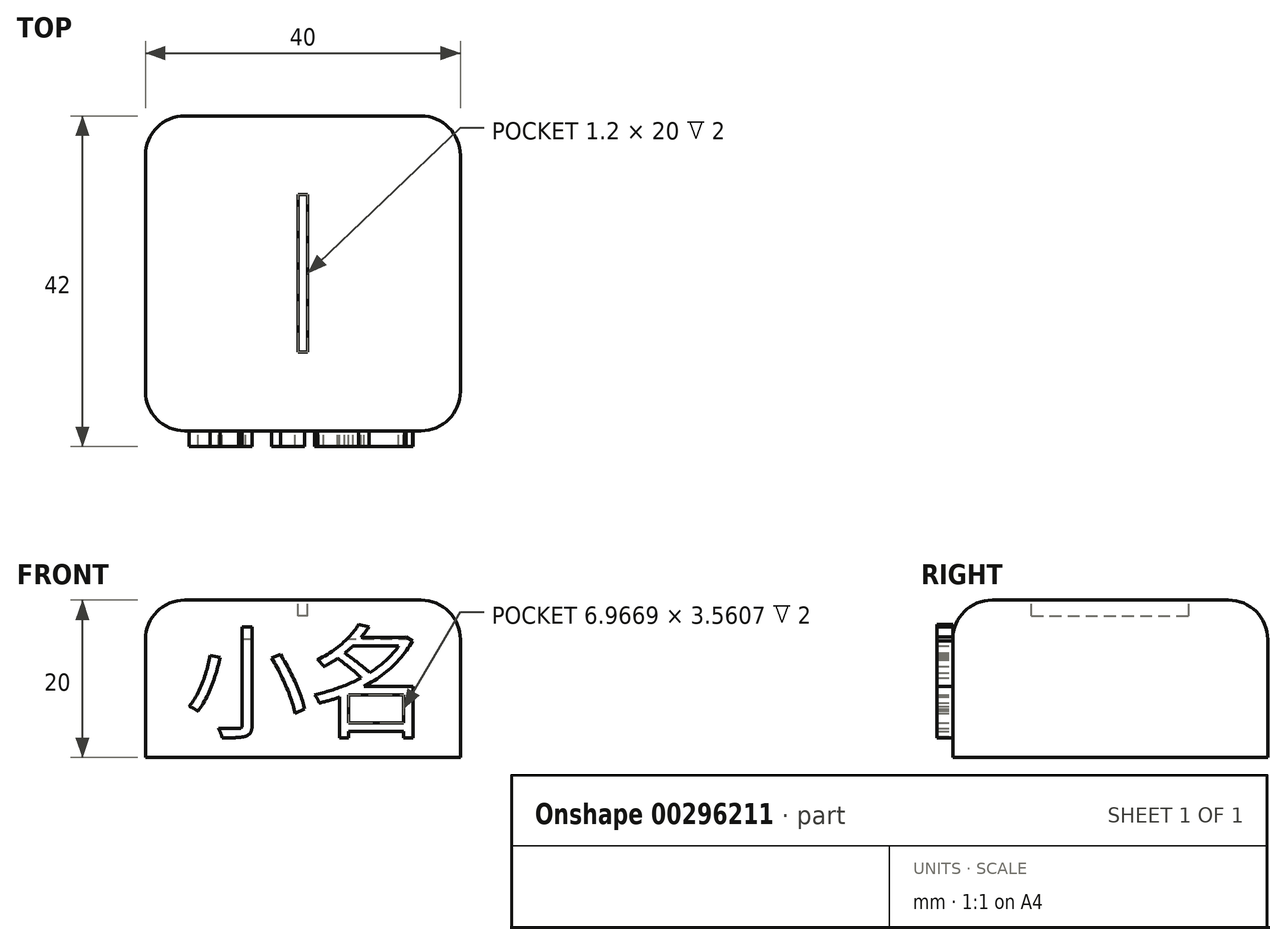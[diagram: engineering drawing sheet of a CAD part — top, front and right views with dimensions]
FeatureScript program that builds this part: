
annotation { "Feature Type Name" : "Feature", "Feature Type Description" : "" }
export const myFeature = defineFeature(function(context is Context, id is Id, definition is map)
    precondition{}
    {
        {
            var Q0;
            Q0=qCreatedBy(makeId("Top.planeOp"),FACE);
            var sketch = newSketch(context, id + "F0", { "sketchPlane" : qUnion([Q0])});
            skLineSegment(sketch, "E0.bottom", {"start": v(20, -20) * mm, "end": v(-20, -20) * mm});
            skLineSegment(sketch, "E0.top", {"start": v(20, 20) * mm, "end": v(-20, 20) * mm});
            skLineSegment(sketch, "E0.left", {"start": v(20, -20) * mm, "end": v(20, 20) * mm});
            skLineSegment(sketch, "E0.right", {"start": v(-20, -20) * mm, "end": v(-20, 20) * mm});
            skPoint(sketch, "E0.middle", {"position": v(0, 0) * mm});
            skLineSegment(sketch, "E1.bottom", {"start": v(0.6, -10) * mm, "end": v(-0.6, -10) * mm});
            skLineSegment(sketch, "E1.top", {"start": v(0.6, 10) * mm, "end": v(-0.6, 10) * mm});
            skLineSegment(sketch, "E1.left", {"start": v(0.6, -10) * mm, "end": v(0.6, 10) * mm});
            skLineSegment(sketch, "E1.right", {"start": v(-0.6, -10) * mm, "end": v(-0.6, 10) * mm});
            skSolve(sketch);
        }
        {
            var Q0;
            Q0=makeQuery(id+"F0.imprint","IMPRINT",FACE,{"disambiguationData":[TD([[makeQuery(id+"F0.imprint","IMPRINT",EDGE,{"derivedFrom":sQuery(id+"F0.wireOp",EDGE,"E0.bottom")}),-1.0]])]});
            var Q1;
            Q1=makeQuery(id+"F0.imprint","IMPRINT",FACE,{"disambiguationData":[TD([[makeQuery(id+"F0.imprint","IMPRINT",EDGE,{"derivedFrom":sQuery(id+"F0.wireOp",EDGE,"E1.bottom")}),-1.0]])]});
            extrude(context, id + "F1", {"entities" : qUnion([Q0, Q1]), "oppositeDirection" : true, "depth" : 20 * mm});
        }
        {
            var Q0;
            Q0=makeQuery(id+"F0.imprint","IMPRINT",FACE,{"disambiguationData":[TD([[makeQuery(id+"F0.imprint","IMPRINT",EDGE,{"derivedFrom":sQuery(id+"F0.wireOp",EDGE,"E1.bottom")}),-1.0]])]});
            extrude(context, id + "F2", {"entities" : qUnion([Q0]), "operationType" : NewBodyOperationType.REMOVE, "oppositeDirection" : true, "depth" : 2 * mm});
        }
        {
            var Q0;
            Q0=makeQuery(id+"F2.boolean.opBoolean","COPY",EDGE,{"derivedFrom":makeQuery(id+"F2.opExtrude","CAP_EDGE",EDGE,{"disambiguationData":[OSD([sQuery(id+"F0.wireOp",EDGE,"E1.left")])],"isStart":true})});
            var Q1;
            Q1=makeQuery(id+"F2.boolean.opBoolean","COPY",EDGE,{"derivedFrom":makeQuery(id+"F2.opExtrude","CAP_EDGE",EDGE,{"disambiguationData":[OSD([sQuery(id+"F0.wireOp",EDGE,"E1.right")])],"isStart":true})});
            var Q2;
            Q2=makeQuery(id+"F1.opExtrude","SWEPT_EDGE",EDGE,{"disambiguationData":[OSD([sQuery(id+"F0.wireOp",EDGE,"E0.bottom"),sQuery(id+"F0.wireOp",EDGE,"E0.left")])]});
            var Q3;
            Q3=makeQuery(id+"F1.opExtrude","SWEPT_EDGE",EDGE,{"disambiguationData":[OSD([sQuery(id+"F0.wireOp",EDGE,"E0.top"),sQuery(id+"F0.wireOp",EDGE,"E0.left")])]});
            var Q4;
            Q4=makeQuery(id+"F1.opExtrude","CAP_EDGE",EDGE,{"disambiguationData":[OSD([sQuery(id+"F0.wireOp",EDGE,"E0.left")])],"isStart":true});
            var Q5;
            Q5=makeQuery(id+"F1.opExtrude","SWEPT_EDGE",EDGE,{"disambiguationData":[OSD([sQuery(id+"F0.wireOp",EDGE,"E0.bottom"),sQuery(id+"F0.wireOp",EDGE,"E0.right")])]});
            var Q6;
            Q6=makeQuery(id+"F1.opExtrude","SWEPT_EDGE",EDGE,{"disambiguationData":[OSD([sQuery(id+"F0.wireOp",EDGE,"E0.top"),sQuery(id+"F0.wireOp",EDGE,"E0.right")])]});
            var Q7;
            Q7=makeQuery(id+"F1.opExtrude","CAP_EDGE",EDGE,{"disambiguationData":[OSD([sQuery(id+"F0.wireOp",EDGE,"E0.top")])],"isStart":true});
            var Q8;
            Q8=makeQuery(id+"F1.opExtrude","CAP_EDGE",EDGE,{"disambiguationData":[OSD([sQuery(id+"F0.wireOp",EDGE,"E0.right")])],"isStart":true});
            var Q9;
            Q9=makeQuery(id+"F1.opExtrude","CAP_EDGE",EDGE,{"disambiguationData":[OSD([sQuery(id+"F0.wireOp",EDGE,"E0.bottom")])],"isStart":true});
            fillet(context, id + "F3", {"entities" : qUnion([Q0, Q1, Q2, Q3, Q4, Q5, Q6, Q7, Q8, Q9]), "radius" : 5 * mm, "tangentPropagation" : true, "allowEdgeOverflow" : false});
        }
        {
            var Q0;
            Q0=makeQuery(id+"F1.opExtrude","SWEPT_FACE",FACE,{"disambiguationData":[OSD([sQuery(id+"F0.wireOp",EDGE,"E0.bottom")])]});
            var sketch = newSketch(context, id + "F4", { "sketchPlane" : qUnion([Q0])});
            skText(sketch, "E2", { "text": "小名", "fontName": "NotoSansCJKtc-Regular.otf"});
            const initialGuessF4  = {"E2": [-0.015, -0.0163, 1, 0, 0.0113]};
            skSetInitialGuess(sketch, initialGuessF4);
            skSolve(sketch);
        }
        {
            var Q0;
            {var subQ0=sQuery(id+"F4.wireOp",EDGE,"E2.sketch_text.stroke-1");Q0=makeQuery(id+"F4.imprint","IMPRINT",FACE,{"disambiguationData":[TD([[makeQuery(id+"F4.imprint","IMPRINT",EDGE,{"derivedFrom":subQ0}),1.0]])]});}
            var Q1;
            Q1=makeQuery(id+"F4.imprint","IMPRINT",FACE,{"disambiguationData":[TD([[makeQuery(id+"F4.imprint","IMPRINT",EDGE,{"derivedFrom":sQuery(id+"F4.wireOp",EDGE,"E2.sketch_text.stroke-12")}),1.0]])]});
            var Q2;
            Q2=makeQuery(id+"F4.imprint","IMPRINT",FACE,{"disambiguationData":[TD([[makeQuery(id+"F4.imprint","IMPRINT",EDGE,{"derivedFrom":sQuery(id+"F4.wireOp",EDGE,"E2.sketch_text.stroke-8")}),1.0]])]});
            var Q3;
            {var subQ0=sQuery(id+"F4.wireOp",EDGE,"E2.sketch_text.stroke-7");Q3=makeQuery(id+"F4.imprint","IMPRINT",FACE,{"disambiguationData":[TD([[makeQuery(id+"F4.imprint","IMPRINT",EDGE,{"derivedFrom":subQ0}),1.0]])]});}
            var Q4;
            Q4=makeQuery(id+"F4.imprint","IMPRINT",FACE,{"disambiguationData":[TD([[makeQuery(id+"F4.imprint","IMPRINT",EDGE,{"derivedFrom":sQuery(id+"F4.wireOp",EDGE,"E2.sketch_text.stroke-16")}),1.0]])]});
            var Q5;
            {var subQ0=sQuery(id+"F4.wireOp",EDGE,"E2.sketch_text.stroke-27");Q5=makeQuery(id+"F4.imprint","IMPRINT",FACE,{"disambiguationData":[TD([[makeQuery(id+"F4.imprint","IMPRINT",EDGE,{"derivedFrom":subQ0}),1.0]])]});}
            extrude(context, id + "F5", {"entities" : qUnion([Q0, Q1, Q2, Q3, Q4, Q5]), "operationType" : NewBodyOperationType.ADD, "depth" : 2 * mm});
        }
    });
